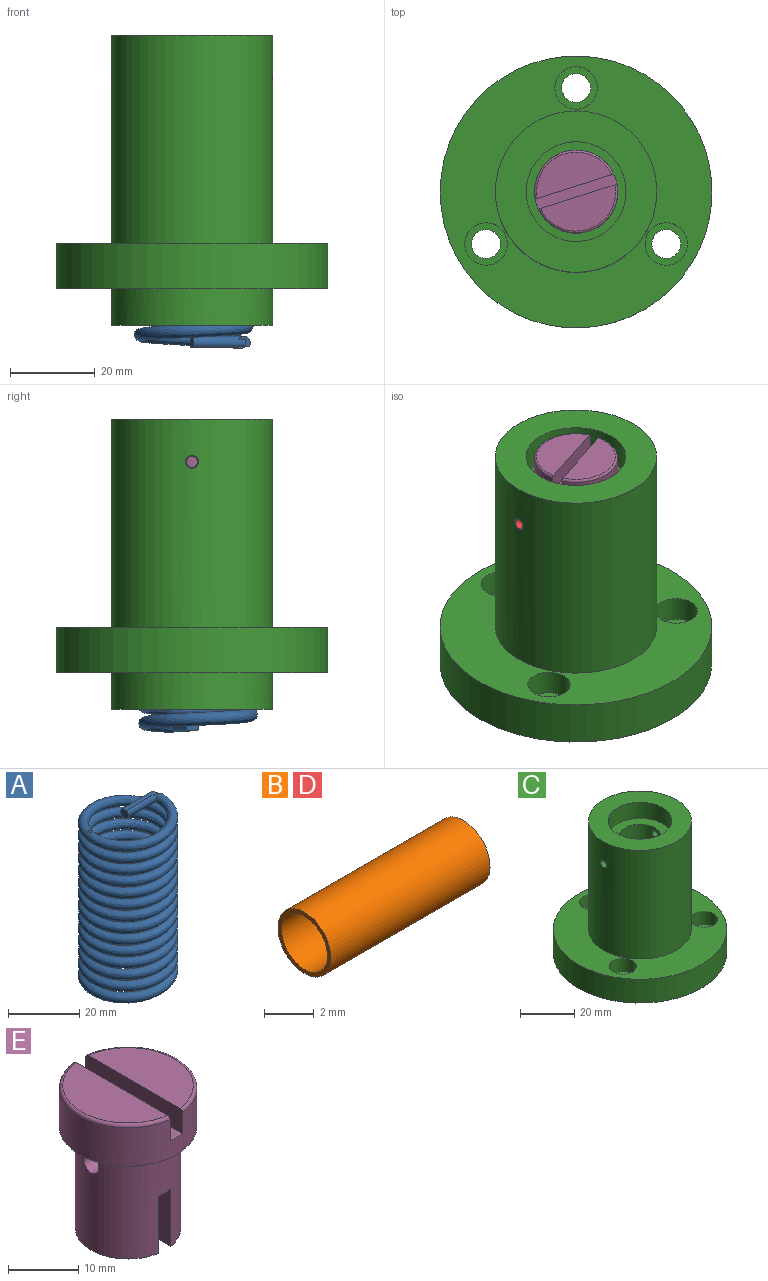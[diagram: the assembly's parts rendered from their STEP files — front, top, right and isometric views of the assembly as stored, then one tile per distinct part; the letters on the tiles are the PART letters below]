
ASSEMBLY  parts=5 mates=4
PART A: 17 faces, bbox 28.2x28x59.8 mm
  f0: bspline ~58.99x27.24mm, area 10412.8mm2, adj f1,f4,f5,f7,f12,f13,f14,f15
  f1: cylinder r=1.5mm len=12.8mm, axis (-1,0,0), area 82mm2, adj f0,f2,f3,f4,f11,f15,f16
  f2: plane 3x2.71mm, normal (-1,0,0), area 6.1mm2, adj f1,f15,f16
  f3: bspline ~10.83x7.75mm, area 0mm2, adj f1,f4,f16
  f4: plane 3.59x3.17mm, normal (0,-1,0), area 3.7mm2, adj f0,f1,f3,f11,f16
  f5: plane 3.62x3.55mm, normal (0,1,0), area 5.5mm2, adj f0,f6,f7
  f6: plane 2.84x2.83mm, normal (1,0,0), area 6.5mm2, adj f5,f7,f9,f10
  f7: cylinder r=1.5mm len=12.2mm, axis (-1,0,0), area 92.1mm2, adj f0,f5,f6,f8,f9,f10
  f8: plane 3x2.84mm, normal (-1,0,0), area 6.6mm2, adj f7,f9,f10
  f9: plane 12.2x0.2mm, normal (0,1,0), area 2.4mm2, adj f6,f7,f8,f10
  f10: plane 12.2x1.65mm, normal (0,0,1), area 20.1mm2, adj f6,f7,f8,f9
  f11: plane 1.39x0.17mm, normal (1,0,0), area 0.2mm2, adj f1,f4
  f12: plane 2.4x0.65mm, normal (0,1,0), area 0.7mm2, adj f0,f14
  f13: plane 2.31x0.57mm, normal (0,-1,0), area 0.6mm2, adj f0,f14
  f14: plane 2.46x1.15mm, normal (0,0,1), area 2.5mm2, adj f0,f12,f13
  f15: plane 13.65x0.7mm, normal (0,-1,0), area 4.1mm2, adj f0,f1,f2,f16
  f16: plane 13.71x2.24mm, normal (0,0,-1), area 28.7mm2, adj f0,f1,f2,f3,f4,f15
PART B: 4 faces, bbox 9x3x3 mm
  f0: plane 3x3mm, normal (-1,0,0), area 1.8mm2, adj f2,f3
  f1: plane 3x3mm, normal (1,0,0), area 1.8mm2, adj f2,f3
  f2: cylinder r=1.5mm len=9mm, axis (-1,0,0), area 84.8mm2, adj f0,f1
  f3: cylinder r=1.3mm len=9mm, axis (1,0,0), area 73.5mm2, adj f0,f1
PART C: 35 faces, bbox 64x64x68.3 mm
  f0: plane 64x64mm, normal (0,0,-1), area 1158.2mm2, adj f3,f4,f7,f8,f9,f16,f17,f18
  f1: plane 64x64mm, normal (0,0,1), area 1847.3mm2, adj f4,f5,f10,f12,f14
  f2: plane 38x38mm, normal (0,0,-1), area 369.6mm2, adj f3,f28
  f3: cylinder r=19mm len=38mm, axis (0,0,-1), area 1576.5mm2, adj f0,f2,f17,f18,f19,f21,f22,f23
  f4: cylinder r=32mm len=64mm, axis (0,0,-1), area 2151.4mm2, adj f0,f1
  f5: cylinder r=19mm len=49mm, axis (0,0,-1), area 5835.5mm2, adj f1,f6,f33,f34
  f6: plane 38x38mm, normal (0,0,1), area 700.4mm2, adj f5,f30
  f7: cylinder r=3.4mm len=6.8mm, axis (0,0,1), area 102.5mm2, adj f0,f15
  f8: cylinder r=3.4mm len=6.8mm, axis (0,0,1), area 102.5mm2, adj f0,f13
  f9: cylinder r=3.4mm len=6.8mm, axis (0,0,1), area 102.5mm2, adj f0,f11
  f10: cylinder r=5mm len=10mm, axis (0,0,1), area 185.4mm2, adj f1,f11
  f11: plane 10x10mm, normal (0,0,1), area 42.2mm2, adj f9,f10
  f12: cylinder r=5mm len=10mm, axis (0,0,1), area 185.4mm2, adj f1,f13
  f13: plane 10x10mm, normal (0,0,1), area 42.2mm2, adj f8,f12
  f14: cylinder r=5mm len=10mm, axis (0,0,1), area 185.4mm2, adj f1,f15
  f15: plane 10x10mm, normal (0,0,1), area 42.2mm2, adj f7,f14
  f16: cylinder r=27.01mm len=32.99mm, axis (0,0,-1), area 305.3mm2, adj f0,f17,f18,f19
  f17: plane 7.31x7.2mm, normal (0.5,0.87,0), area 60.7mm2, adj f0,f3,f16,f19
  f18: plane 8.41x7.2mm, normal (1,0,0), area 60.6mm2, adj f0,f3,f16,f19
  f19: plane 32.99x20.11mm, normal (0,0,-1), area 272mm2, adj f3,f16,f17,f18
  f20: cylinder r=27.01mm len=33.15mm, axis (0,0,-1), area 305.4mm2, adj f0,f21,f22,f23
  f21: plane 8.44x7.2mm, normal (-1,0,0), area 60.7mm2, adj f0,f3,f20,f23
  f22: plane 7.28x7.2mm, normal (-0.5,0.86,0), area 60.7mm2, adj f0,f3,f20,f23
  f23: plane 33.15x19.91mm, normal (0,0,-1), area 271.8mm2, adj f3,f20,f21,f22
  f24: plane 7.31x7.2mm, normal (-0.5,-0.87,0), area 60.7mm2, adj f0,f3,f25,f27
  f25: cylinder r=27.01mm len=38.18mm, axis (0,0,-1), area 305.3mm2, adj f0,f24,f26,f27
  f26: plane 7.28x7.2mm, normal (0.5,-0.86,0), area 60.7mm2, adj f0,f3,f25,f27
  f27: plane 38.18x12.16mm, normal (0,0,-1), area 271.9mm2, adj f3,f24,f25,f26
  f28: cylinder r=15.6mm len=52mm, axis (0,0,-1), area 5096.9mm2, adj f2,f29
  f29: plane 31.2x31.2mm, normal (0,0,-1), area 568.5mm2, adj f28,f32
  f30: cylinder r=11.75mm len=23.5mm, axis (0,0,1), area 531.6mm2, adj f6,f31
  f31: plane 23.5x23.5mm, normal (0,0,1), area 237.7mm2, adj f30,f32
  f32: cylinder r=7.9mm len=15.8mm, axis (0,0,1), area 437.5mm2, adj f29,f31,f33,f34
  f33: cylinder r=1.5mm len=11.24mm, axis (1,0,0), area 105mm2, adj f5,f32
  f34: cylinder r=1.5mm len=11.24mm, axis (1,0,0), area 105mm2, adj f5,f32
PART D: same geometry as B
PART E: 16 faces, bbox 21.2x21x25 mm
  f0: cylinder r=7.5mm len=17.8mm, axis (0,0,1), area 774.4mm2, adj f1,f4,f5,f12,f13,f14,f15
  f1: plane 14.79x6.25mm, normal (0,0,-1), area 69.7mm2, adj f0,f13
  f2: cylinder r=9.8mm len=19.6mm, axis (0,0,1), area 394mm2, adj f5,f7,f8,f9,f10,f11
  f3: plane 18.43x8.05mm, normal (0,0,1), area 112.7mm2, adj f9,f11
  f4: plane 14.79x6.25mm, normal (0,0,-1), area 69.7mm2, adj f0,f12
  f5: plane 19.6x19.6mm, normal (0,0,-1), area 125mm2, adj f0,f2
  f6: plane 18.43x8.05mm, normal (0,0,1), area 112.7mm2, adj f8,f10
  f7: plane 19.6x2.5mm, normal (0,0,1), area 48.9mm2, adj f2,f8,f9
  f8: plane 19.44x4.2mm, normal (-1,0,0), area 81.5mm2, adj f2,f6,f7,f10
  f9: plane 19.44x4.2mm, normal (1,0,0), area 81.5mm2, adj f2,f3,f7,f11
  f10: torus R=9.3mm, axis (0,0,-1), area 21.8mm2, adj f2,f6,f8
  f11: torus R=9.3mm, axis (0,0,-1), area 21.8mm2, adj f2,f3,f9
  f12: plane 14.79x10mm, normal (-1,0,0), area 147.9mm2, adj f0,f4,f14
  f13: plane 14.79x10mm, normal (1,0,0), area 147.9mm2, adj f0,f1,f14
  f14: plane 15x2.5mm, normal (0,0,-1), area 37.3mm2, adj f0,f12,f13
  f15: cylinder r=1.5mm len=15mm, axis (-1,0,0), area 139.9mm2, adj f0
PLACE A rot(axis=(0,0,1),17.7deg) t=(-35.83,-22.83,-13.01)mm
PLACE B t=(-26.22,-21.39,49.36)mm
PLACE C t=(-36.19,-21.39,-8.94)mm fixed
PLACE D t=(-55.15,-21.39,49.36)mm
PLACE E rot(axis=(0,0,-1),72.3deg) t=(-36.19,-21.39,34.36)mm
MATE fastened D.f2 <-> C.f33  axis (-1,0,0) through (-50.65,-21.39,49.36)mm
MATE revolute E.f0 <-> C.f3  axis (0,0,-1) through (-36.19,-21.39,52.16)mm
MATE fastened E.f0 <-> A.f10  axis (0,0,-1) through (-36.19,-21.39,44.36)mm
MATE fastened B.f2 <-> C.f33  axis (-1,0,0) through (-21.72,-21.39,49.36)mm
